# Revit family: Shower-Bath_and_Shower_Trim-KOHLER-Fairfax-K-TLS12007
name_source: partatom
category: Plumbing Fixtures
revit_build: Autodesk Revit 2015 (Build: 20140606_1530(x64)
units: mm (PartAtom-declared; Revit-internal decimal feet)

## types (6) — shared parameters
ADA Compliant = No
Assembly Code = D2010700
CW Connection = No
Date Modified = 02/06/2019
Default Elevation = 42"
Drain Included = No
HW Connection = Yes
Height = 6 1/2"
Length = 4 3/8"
Manufacturer = KOHLER Co.
MasterFormat 1995 = 15410
MasterFormat 2004 = 22.41.23
Material = Premium Metal Construction
Product Documentation Link = https://www.us.kohler.com
Product Name = Fairfax
Product Page URL = http://www.us.kohler.com
Tempered Water Inlet 1 = Tempered Water Inlet 1
Tempered Water Inlet 2 = Tempered Water Inlet 2
URL = https://www.us.kohler.com
Vent Connection = No
Waste Connection = No
Waste Water Outlet = Waste Water Outlet
WaterSense Certified = No
Width = 6 1/2"

## per-type parameters (varying)
| type | Connector Diameter of Spout | Description | Finish | Model | Slip-Fit Spout 5/8 Inch OD | Threaded Spout 1/2 Inch OD | Type |
| Threaded Spout, 1/2 Inch OD, CP-Polished Chrome | 1/2" | Rite-Temp bath and shower trim set with NPT spout, less showerhead | Kohler-Metal-CP-Polished_Chrome | K-TLS12007-4-CP | No | Yes | 1 |
| Threaded Spout, 1/2 Inch OD, BN-Vibrant Brushed Nickel | 1/2" | Rite-Temp bath and shower trim set with NPT spout, less showerhead | Kohler-Metal-BN-Vibrant_Brushed_Nickel | K-TLS12007-4-BN | No | Yes | 2 |
| Threaded Spout, 1/2 Inch OD, 2BZ-Oil Rubbed Bronze | 1/2" | Rite-Temp bath and shower trim set with NPT spout, less showerhead | Kohler-Metal-2BZ-Oil_Rubbed_Bronze | K-TLS12007-4-2BZ | No | Yes | 3 |
| Slip Fit Spout, 5/8 Inch OD, CP-Polished Chrome | 5/8" | Rite-Temp bath and shower trim set with lever handle and slip-fit spout, less showerhead | Kohler-Metal-CP-Polished_Chrome | K-TLS12007-4S-CP | Yes | No | 4 |
| Slip Fit Spout, 5/8 Inch OD, BN-Vibrant Brushed Nickel | 5/8" | Rite-Temp bath and shower trim set with lever handle and slip-fit spout, less showerhead | Kohler-Metal-BN-Vibrant_Brushed_Nickel | K-TLS12007-4S-BN | Yes | No | 5 |
| Slip Fit Spout, 5/8 Inch OD, 2BZ-Oil Rubbed Bronze | 5/8" | Rite-Temp bath and shower trim set with lever handle and slip-fit spout, less showerhead | Kohler-Metal-2BZ-Oil_Rubbed_Bronze | K-TLS12007-4S-2BZ | Yes | No | 6 |

## geometry (parser evidence)
native form markers: Sweep x12
no freeform markers — native parametric forms only
